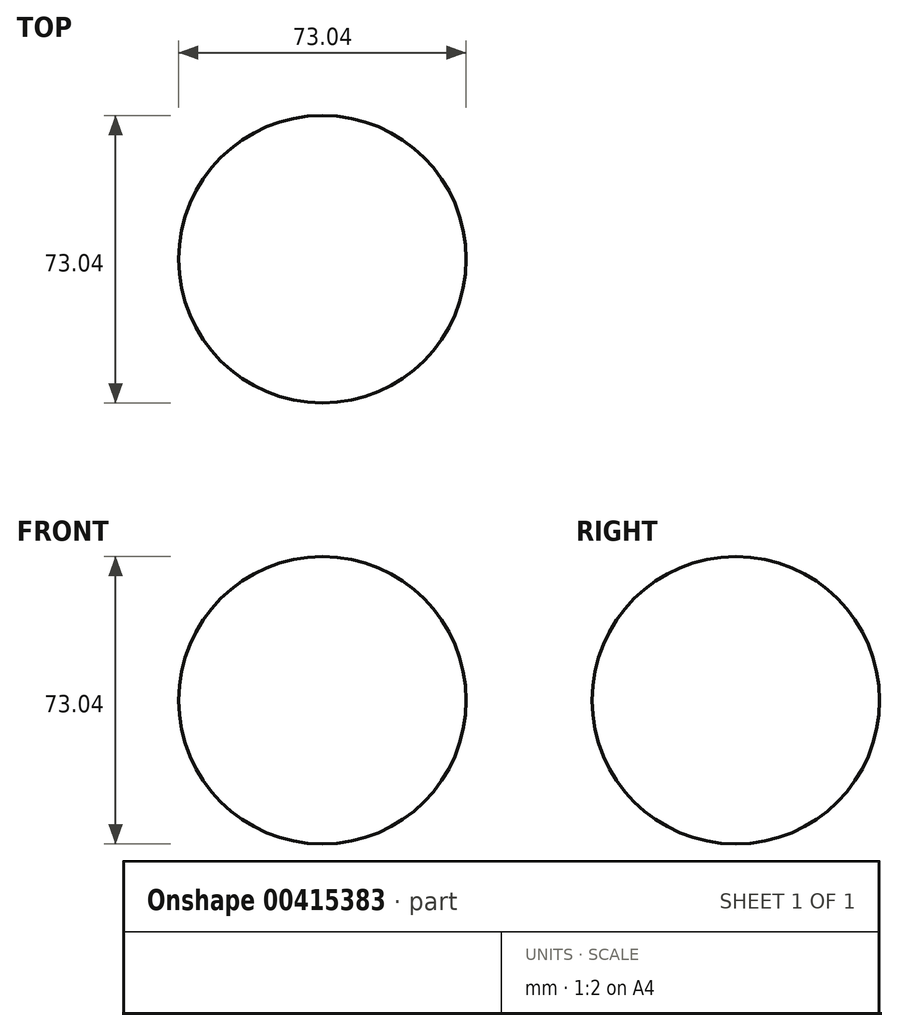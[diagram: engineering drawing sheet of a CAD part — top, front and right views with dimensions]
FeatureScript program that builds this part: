
annotation { "Feature Type Name" : "Feature", "Feature Type Description" : "" }
export const myFeature = defineFeature(function(context is Context, id is Id, definition is map)
    precondition{}
    {
        {
            var Q0;
            Q0=qCreatedBy(makeId("Front.planeOp"),FACE);
            var sketch = newSketch(context, id + "F0", { "sketchPlane" : qUnion([Q0])});
            skArc(sketch, "E0", {"start": v(0, 36.52) * mm, "mid": v(-36.52, 0) * mm, "end": v(0, -36.52) * mm});
            skLineSegment(sketch, "E1", {"start": v(0, 36.52) * mm, "end": v(0, -36.52) * mm});
            skSolve(sketch);
        }
        {
            var Q0;
            Q0=makeQuery(id+"F0.imprint","IMPRINT",FACE,{"disambiguationData":[TD([[makeQuery(id+"F0.imprint","IMPRINT",EDGE,{"derivedFrom":sQuery(id+"F0.wireOp",EDGE,"E0")}),1.0]])]});
            var Q1;
            Q1=sQuery(id+"F0.wireOp",EDGE,"E1");
            revolve(context, id + "F1", {"entities" : qUnion([Q0]), "axis" : qUnion([Q1]), "revolveType" : RevolveType.FULL});
        }
    });
